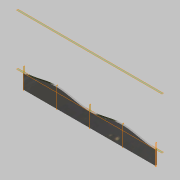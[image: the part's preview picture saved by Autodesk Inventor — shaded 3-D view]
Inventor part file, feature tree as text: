
AUTODESK INVENTOR PART (.ipt)
format: ipt  version: 2017.3 (Build 213257000, 257)  size: 168,960 bytes
history: native  units: in
note: dims shown in document units (in); Inventor stores cm internally (conversion verified against a paired STEP export)
features: plane x7, extrude x2, sketch x2, other x2
ambient origin geometry x8: Origin, YZ Plane, XZ Plane, XY Plane, X Axis, Y Axis, Z Axis, Center Point
bodies: Solid1 (feature_tree)
feature tree (13):
  extrude  "Extrusion1"  Depth=0.5in TaperAngle=0.0deg
  extrude  "Extrusion2"  Depth=0.001in TaperAngle=0.0deg
  plane  "Work Plane1 Centerline at surface"
  plane  "Work Plane2 Centerline at centerline"
  plane  "Work Plane3 Top"
  plane  "Work Plane4 Right"
  plane  "Work Plane5 Bottom"
  plane  "Work Plane6 Left"
  plane  "Work Plane7 Top"
  sketch  "Sketch1"  dims[d0=0.0in d1=17.3159in d2=0.5in d3=0.0in]
  other  "2D Equation Curve1"
  sketch  "Sketch2"  dims[d4=0.0in d5=17.3159in d6=0.001in d7=0.0in d8=-4.753in d9=-21.753in d10=0.0in d11=-10.9956in d12=-21.9911in d13=-32.9867in d14=0.0in]
  other  "2D Equation Curve2"
